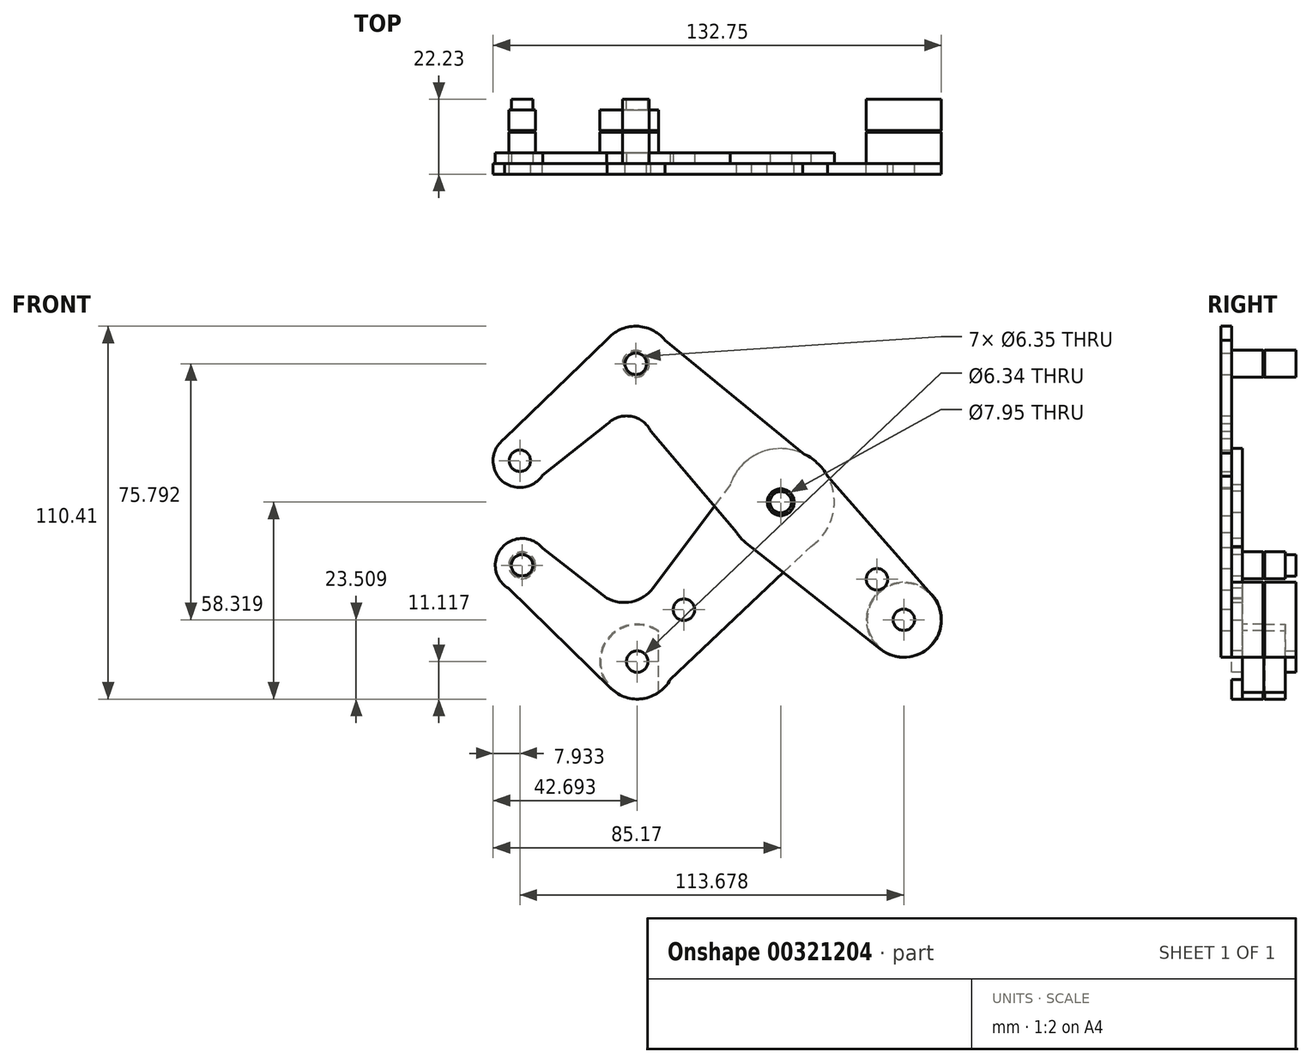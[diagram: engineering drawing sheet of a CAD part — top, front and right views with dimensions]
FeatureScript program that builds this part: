
annotation { "Feature Type Name" : "Feature", "Feature Type Description" : "" }
export const myFeature = defineFeature(function(context is Context, id is Id, definition is map)
    precondition{}
    {
        {
            var Q0;
            Q0=qCreatedBy(makeId("Front.planeOp"),FACE);
            var sketch = newSketch(context, id + "F0", { "sketchPlane" : qUnion([Q0])});
            skLineSegment(sketch, "E0", {"start": v(-73.2, 40.63) * mm, "end": v(-38.86, 69.35) * mm, "construction": true});
            skLineSegment(sketch, "E1", {"start": v(-38.86, 69.35) * mm, "end": v(4.04, 28.37) * mm, "construction": true});
            skLineSegment(sketch, "E2", {"start": v(4.04, 28.37) * mm, "end": v(40.48, -6.44) * mm, "construction": true});
            skCircle(sketch, "E3", {"center": v(-38.86, 69.35) * mm, "radius": 11.11 * mm});
            skCircle(sketch, "E4", {"center": v(-73.2, 40.63) * mm, "radius": 7.94 * mm});
            skCircle(sketch, "E5", {"center": v(4.04, 28.37) * mm, "radius": 15.88 * mm});
            skCircle(sketch, "E6", {"center": v(40.48, -6.44) * mm, "radius": 11.11 * mm});
            skCircle(sketch, "E7", {"center": v(40.48, -6.44) * mm, "radius": 3.18 * mm});
            skCircle(sketch, "E8", {"center": v(-73.2, 40.63) * mm, "radius": 3.18 * mm});
            skCircle(sketch, "E9", {"center": v(-38.86, 69.35) * mm, "radius": 3.18 * mm});
            skCircle(sketch, "E10", {"center": v(4.04, 28.37) * mm, "radius": 3.98 * mm});
            skCircle(sketch, "E11", {"center": v(32.54, 5.53) * mm, "radius": 3.18 * mm});
            skLineSegment(sketch, "E12", {"start": v(-77.69, 47.17) * mm, "end": v(-45.74, 78.08) * mm});
            skLineSegment(sketch, "E13", {"start": v(-33.66, 79.17) * mm, "end": v(10.53, 42.86) * mm});
            skLineSegment(sketch, "E14", {"start": v(13.4, 41.2) * mm, "end": v(48.83, 0.9) * mm});
            skLineSegment(sketch, "E15", {"start": v(-66.52, 36.34) * mm, "end": v(-47.14, 51.63) * mm});
            skLineSegment(sketch, "E16", {"start": v(-34.43, 49.4) * mm, "end": v(-6.96, 16.92) * mm});
            skLineSegment(sketch, "E17", {"start": v(-6.96, 16.92) * mm, "end": v(33.59, -15.16) * mm});
            skArc(sketch, "E18", {"start": v(-34.43, 49.4) * mm, "mid": v(-40.21, 53.77) * mm, "end": v(-47.14, 51.63) * mm});
            skSolve(sketch);
        }
        {
            var Q0;
            Q0=qCreatedBy(makeId("Front.planeOp"),FACE);
            var sketch = newSketch(context, id + "F1", { "sketchPlane" : qUnion([Q0])});
            skLineSegment(sketch, "E19", {"start": v(4.04, 28.37) * mm, "end": v(-38.44, -18.83) * mm, "construction": true});
            skLineSegment(sketch, "E20", {"start": v(-38.44, -18.83) * mm, "end": v(-72.54, 9.68) * mm, "construction": true});
            skCircle(sketch, "E21", {"center": v(-38.44, -18.83) * mm, "radius": 11.11 * mm});
            skCircle(sketch, "E22", {"center": v(-72.54, 9.68) * mm, "radius": 7.94 * mm});
            skCircle(sketch, "E23", {"center": v(-38.44, -18.83) * mm, "radius": 3.17 * mm});
            skCircle(sketch, "E24", {"center": v(-72.54, 9.68) * mm, "radius": 3.18 * mm});
            skCircle(sketch, "E25", {"center": v(4.04, 28.37) * mm, "radius": 3.18 * mm});
            skCircle(sketch, "E26", {"center": v(-24.62, -3.48) * mm, "radius": 3.18 * mm});
            skLineSegment(sketch, "E27", {"start": v(-79.27, 5.47) * mm, "end": v(-46.2, -26.79) * mm});
            skLineSegment(sketch, "E28", {"start": v(-28.69, -24.16) * mm, "end": v(13, 15.26) * mm});
            skLineSegment(sketch, "E29", {"start": v(-69.22, 16.88) * mm, "end": v(-47.55, 0) * mm});
            skLineSegment(sketch, "E30", {"start": v(-10.97, 33.54) * mm, "end": v(-33.74, 2.96) * mm});
            skArc(sketch, "E31", {"start": v(-47.55, 0) * mm, "mid": v(-40.09, -1.12) * mm, "end": v(-33.74, 2.96) * mm});
            skCircle(sketch, "E32", {"center": v(4.04, 28.37) * mm, "radius": 15.88 * mm});
            skSolve(sketch);
        }
        {
            var Q0;
            Q0 = qSketchRegion(id + "F0", true);
            extrude(context, id + "F2", {"entities" : qUnion([Q0]), "depth" : 3.17 * mm});
        }
        {
            var Q0;
            Q0 = qSketchRegion(id + "F1", true);
            extrude(context, id + "F3", {"entities" : qUnion([Q0]), "oppositeDirection" : true, "depth" : 3.17 * mm});
        }
        {
            var Q0;
            Q0=qCreatedBy(makeId("Front.planeOp"),FACE);
            var sketch = newSketch(context, id + "F4", { "sketchPlane" : qUnion([Q0])});
            skCircle(sketch, "E33", {"center": v(-38.86, 69.35) * mm, "radius": 3.98 * mm});
            skCircle(sketch, "E34", {"center": v(40.5, -6.45) * mm, "radius": 11.11 * mm});
            skArc(sketch, "E35", {"start": v(-32.09, -9.71) * mm, "mid": v(-49.55, -18.83) * mm, "end": v(-32.09, -27.95) * mm});
            skLineSegment(sketch, "E36", {"start": v(-32.09, -9.71) * mm, "end": v(-32.09, -27.95) * mm});
            skPoint(sketch, "E37", {"position": v(-32.09, -18.83) * mm});
            skLineSegment(sketch, "E38", {"start": v(-32.09, -18.83) * mm, "end": v(40.5, -6.45) * mm, "construction": true});
            skCircle(sketch, "E39", {"center": v(-72.54, 9.68) * mm, "radius": 3.98 * mm});
            skSolve(sketch);
        }
        {
            var Q0;
            Q0=qCreatedBy(makeId("Front.planeOp"),FACE);
            cPlane(context, id + "F5", {"entities" : qUnion([Q0]), "cplaneType" : CPlaneType.OFFSET, "offset" : 9.52 * mm, "oppositeDirection" : true, "width" : 152.4 * mm, "height" : 152.4 * mm});
        }
        {
            var Q0;
            Q0 = qSketchRegion(id + "F4", true);
            var Q1;
            Q1=qCreatedBy(id+"F5.planeOp",FACE);
            extrude(context, id + "F6", {"entities" : qUnion([Q0]), "endBound" : BoundingType.UP_TO_SURFACE, "oppositeDirection" : true, "endBoundEntityFace" : qUnion([Q1]), "depth" : 25.4 * mm});
        }
        {
            var Q0;
            Q0=makeQuery(id+"F2.opExtrude","SWEPT_BODY",BODY,{"disambiguationData":[OSD([sQuery(id+"F0.wireOp",EDGE,"E3"),sQuery(id+"F0.wireOp",EDGE,"E4"),sQuery(id+"F0.wireOp",EDGE,"E5"),sQuery(id+"F0.wireOp",EDGE,"E6"),sQuery(id+"F0.wireOp",EDGE,"E7"),sQuery(id+"F0.wireOp",EDGE,"E8"),sQuery(id+"F0.wireOp",EDGE,"E9"),sQuery(id+"F0.wireOp",EDGE,"E10"),sQuery(id+"F0.wireOp",EDGE,"E11"),sQuery(id+"F0.wireOp",EDGE,"E12"),sQuery(id+"F0.wireOp",EDGE,"E13"),sQuery(id+"F0.wireOp",EDGE,"E14"),sQuery(id+"F0.wireOp",EDGE,"E15"),sQuery(id+"F0.wireOp",EDGE,"E16"),sQuery(id+"F0.wireOp",EDGE,"E17"),sQuery(id+"F0.wireOp",EDGE,"E18")])]});
            var Q1;
            Q1=makeQuery(id+"F3.opExtrude","SWEPT_BODY",BODY,{"disambiguationData":[OSD([sQuery(id+"F1.wireOp",EDGE,"E21"),sQuery(id+"F1.wireOp",EDGE,"E22"),sQuery(id+"F1.wireOp",EDGE,"E23"),sQuery(id+"F1.wireOp",EDGE,"E24"),sQuery(id+"F1.wireOp",EDGE,"E25"),sQuery(id+"F1.wireOp",EDGE,"E26"),sQuery(id+"F1.wireOp",EDGE,"E27"),sQuery(id+"F1.wireOp",EDGE,"E28"),sQuery(id+"F1.wireOp",EDGE,"E29"),sQuery(id+"F1.wireOp",EDGE,"E30"),sQuery(id+"F1.wireOp",EDGE,"E31"),sQuery(id+"F1.wireOp",EDGE,"E32")])]});
            var Q2;
            Q2=makeQuery(id+"F6.opExtrude","SWEPT_BODY",BODY,{"disambiguationData":[OSD([sQuery(id+"F4.wireOp",EDGE,"E33")])]});
            var Q3;
            Q3=makeQuery(id+"F6.opExtrude","SWEPT_BODY",BODY,{"disambiguationData":[OSD([sQuery(id+"F4.wireOp",EDGE,"E39")])]});
            var Q4;
            Q4=makeQuery(id+"F6.opExtrude","SWEPT_BODY",BODY,{"disambiguationData":[OSD([sQuery(id+"F4.wireOp",EDGE,"E35"),sQuery(id+"F4.wireOp",EDGE,"E36")])]});
            var Q5;
            Q5=makeQuery(id+"F6.opExtrude","SWEPT_BODY",BODY,{"disambiguationData":[OSD([sQuery(id+"F4.wireOp",EDGE,"E34")])]});
            booleanBodies(context, id + "F7", {"operationType" : BooleanOperationType.SUBTRACTION, "tools" : qUnion([Q0, Q1]), "targets" : qUnion([Q2, Q3, Q4, Q5]), "keepTools" : true});
        }
        {
            var Q0;
            Q0=makeQuery(id+"F6.opExtrude","CAP_FACE",FACE,{"disambiguationData":[OSD([sQuery(id+"F4.wireOp",EDGE,"E33")])],"isStart":false});
            var Q1;
            Q1=makeQuery(id+"F6.opExtrude","CAP_EDGE",EDGE,{"disambiguationData":[OSD([sQuery(id+"F4.wireOp",EDGE,"E39")])],"isStart":false});
            var Q2;
            Q2=makeQuery(id+"F6.opExtrude","CAP_EDGE",EDGE,{"disambiguationData":[OSD([sQuery(id+"F4.wireOp",EDGE,"E35")])],"isStart":false});
            var Q3;
            Q3=makeQuery(id+"F6.opExtrude","CAP_EDGE",EDGE,{"disambiguationData":[OSD([sQuery(id+"F4.wireOp",EDGE,"E34")])],"isStart":false});
            chamfer(context, id + "F8", {"entities" : qUnion([Q0, Q1, Q2, Q3]), "width" : 0.25 * mm, "tangentPropagation" : true});
        }
        {
            var Q0;
            Q0=makeQuery(id+"F6.opExtrude","SWEPT_BODY",BODY,{"disambiguationData":[OSD([sQuery(id+"F4.wireOp",EDGE,"E33")])]});
            var Q1;
            Q1=makeQuery(id+"F6.opExtrude","SWEPT_BODY",BODY,{"disambiguationData":[OSD([sQuery(id+"F4.wireOp",EDGE,"E39")])]});
            var Q2;
            Q2=makeQuery(id+"F6.opExtrude","SWEPT_BODY",BODY,{"disambiguationData":[OSD([sQuery(id+"F4.wireOp",EDGE,"E35"),sQuery(id+"F4.wireOp",EDGE,"E36")])]});
            var Q3;
            Q3=makeQuery(id+"F6.opExtrude","SWEPT_BODY",BODY,{"disambiguationData":[OSD([sQuery(id+"F4.wireOp",EDGE,"E34")])]});
            var Q4;
            Q4=qCreatedBy(id+"F5.planeOp",FACE);
            mirror(context, id + "F9", {"entities" : qUnion([Q0, Q1, Q2, Q3]), "mirrorPlane" : qUnion([Q4])});
        }
    });
